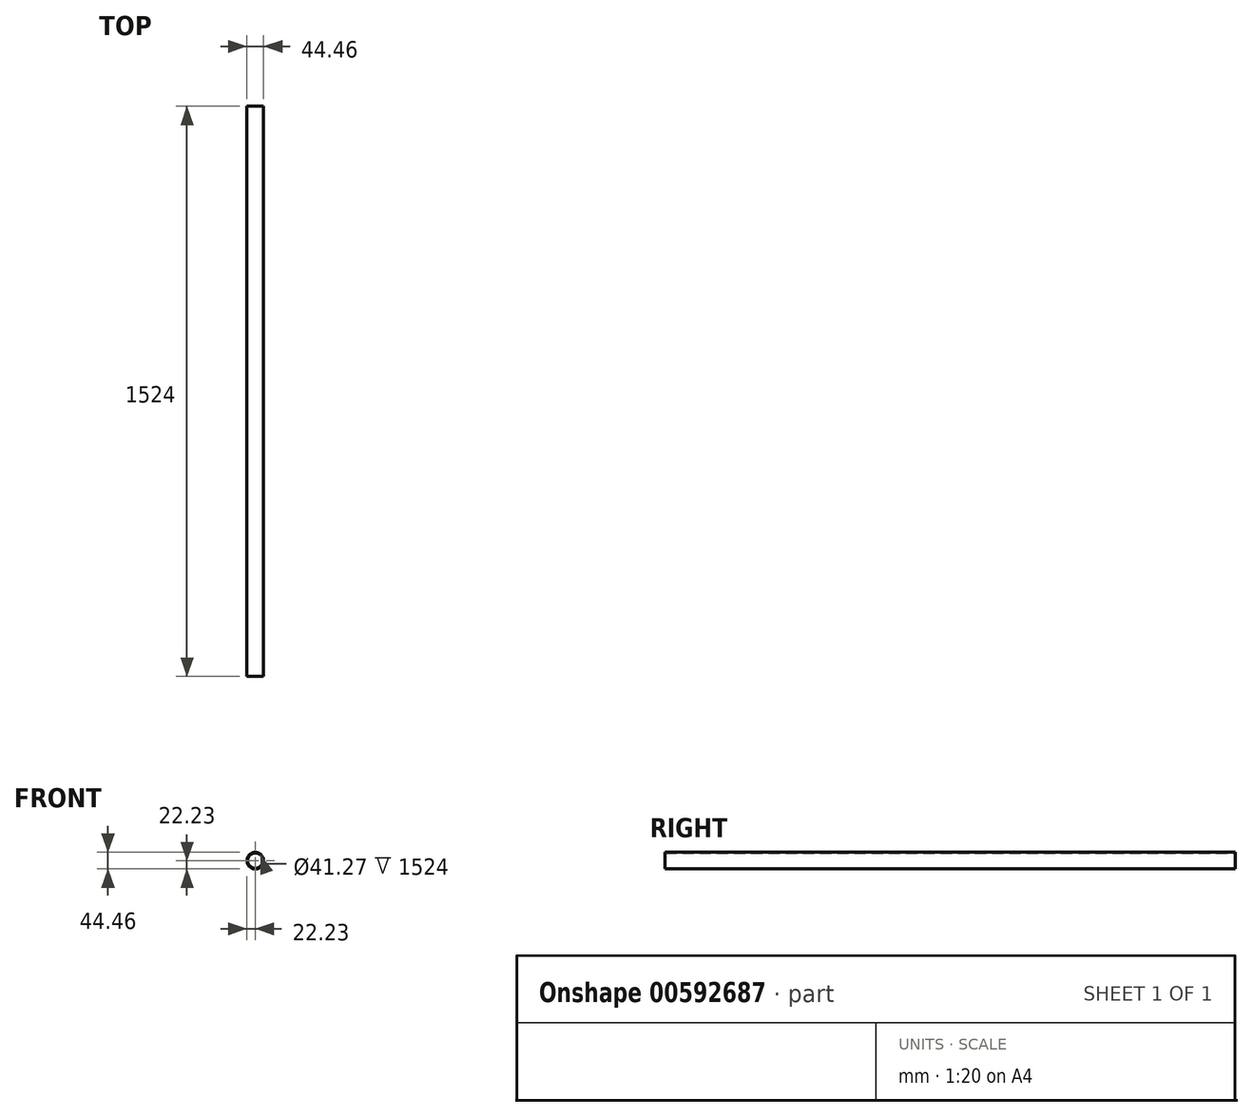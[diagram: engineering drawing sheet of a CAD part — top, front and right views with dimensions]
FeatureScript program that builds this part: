
annotation { "Feature Type Name" : "Feature", "Feature Type Description" : "" }
export const myFeature = defineFeature(function(context is Context, id is Id, definition is map)
    precondition{}
    {
        {
            var Q0;
            Q0=qCreatedBy(makeId("Front.planeOp"),FACE);
            var sketch = newSketch(context, id + "F0", { "sketchPlane" : qUnion([Q0])});
            skCircle(sketch, "E0", {"center": v(0, 0) * mm, "radius": 22.23 * mm});
            skCircle(sketch, "E1", {"center": v(0, 0) * mm, "radius": 20.64 * mm});
            skSolve(sketch);
        }
        {
            var Q0;
            Q0 = qSketchRegion(id + "F0", true);
            extrude(context, id + "F1", {"entities" : qUnion([Q0]), "depth" : 1524 * mm, "offsetDistance" : 25.4 * mm});
        }
    });
